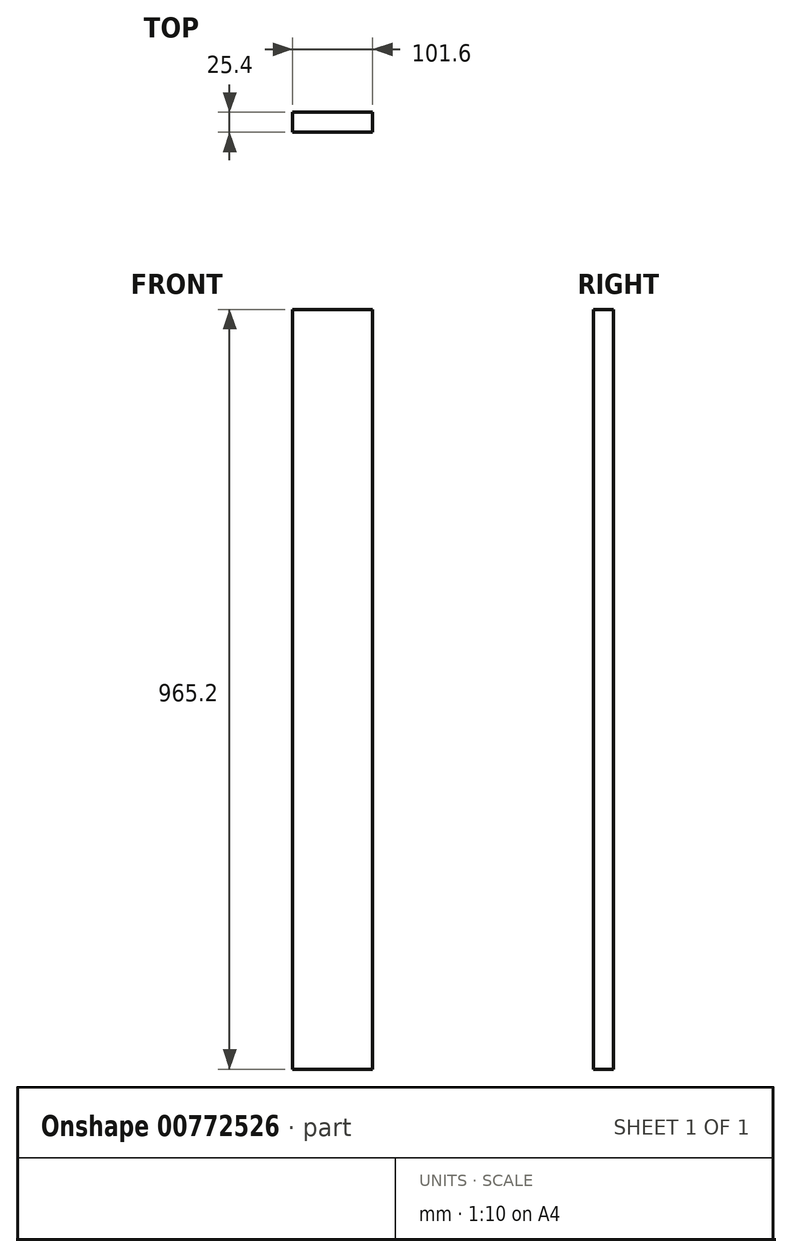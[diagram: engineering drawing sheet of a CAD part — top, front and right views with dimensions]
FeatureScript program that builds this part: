
annotation { "Feature Type Name" : "Feature", "Feature Type Description" : "" }
export const myFeature = defineFeature(function(context is Context, id is Id, definition is map)
    precondition{}
    {
        {
            var Q0;
            Q0=qCreatedBy(makeId("Front.planeOp"),FACE);
            var sketch = newSketch(context, id + "F0", { "sketchPlane" : qUnion([Q0])});
            skLineSegment(sketch, "E0.bottom", {"start": v(-50.8, 482.6) * mm, "end": v(50.8, 482.6) * mm});
            skLineSegment(sketch, "E0.top", {"start": v(-50.8, -482.6) * mm, "end": v(50.8, -482.6) * mm});
            skLineSegment(sketch, "E0.left", {"start": v(-50.8, 482.6) * mm, "end": v(-50.8, -482.6) * mm});
            skLineSegment(sketch, "E0.right", {"start": v(50.8, 482.6) * mm, "end": v(50.8, -482.6) * mm});
            skSolve(sketch);
        }
        {
            var Q0;
            Q0=qSketchRegion(id+"F0",true);
            extrude(context, id + "F1", {"entities" : qUnion([Q0]), "oppositeDirection" : true, "depth" : 25.4 * mm, "offsetDistance" : 25.4 * mm});
        }
    });
